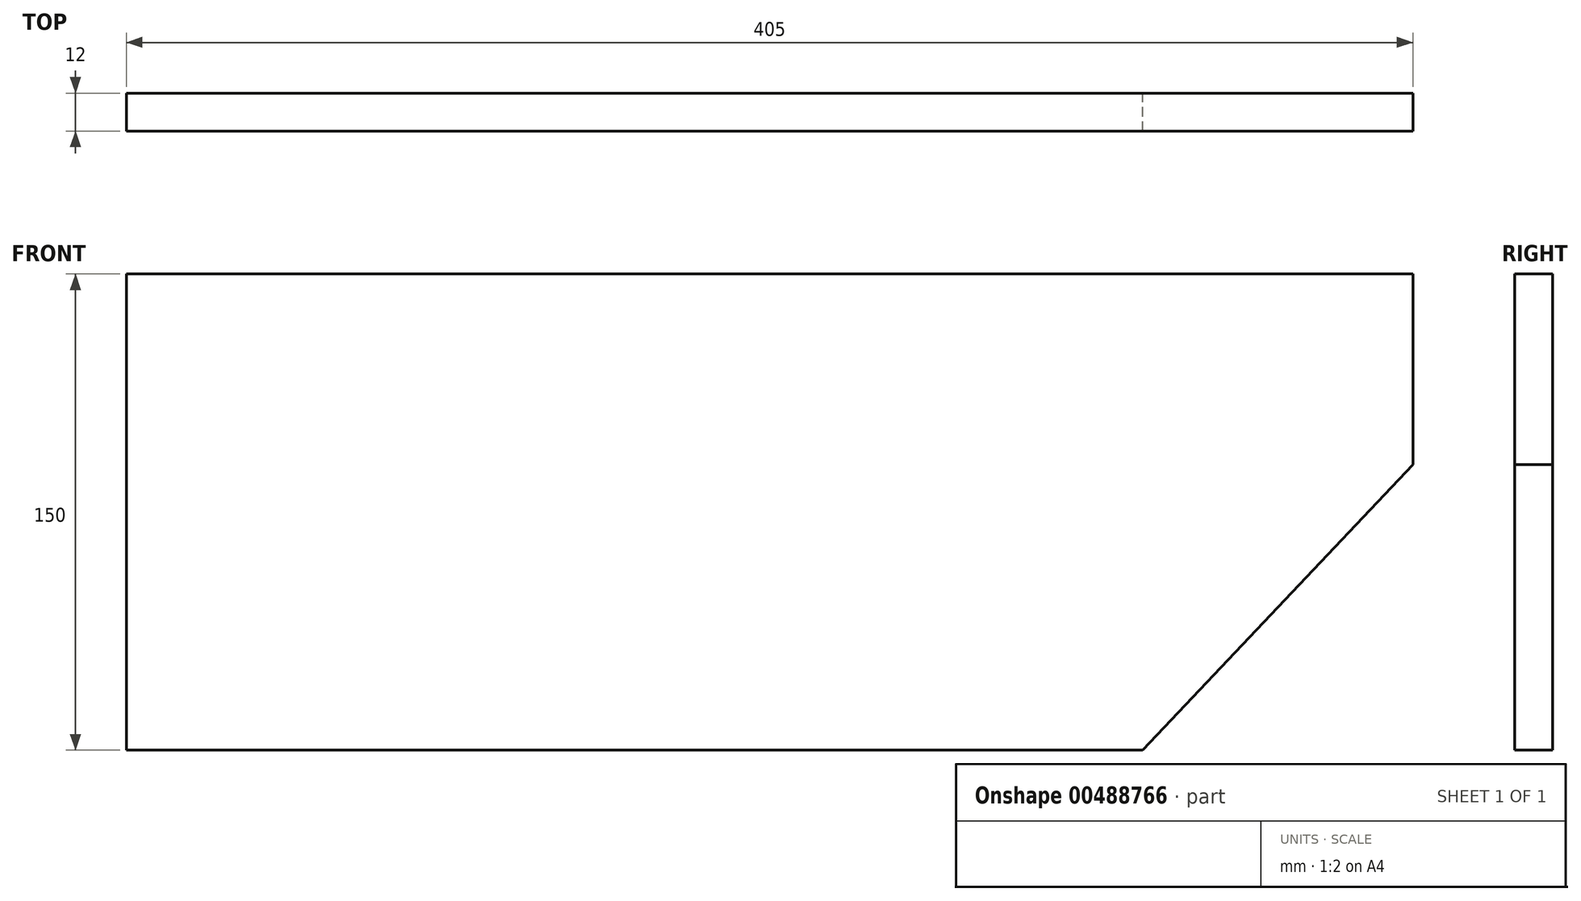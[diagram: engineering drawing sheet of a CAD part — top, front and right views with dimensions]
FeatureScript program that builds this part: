
annotation { "Feature Type Name" : "Feature", "Feature Type Description" : "" }
export const myFeature = defineFeature(function(context is Context, id is Id, definition is map)
    precondition{}
    {
        {
            var Q0;
            Q0=qCreatedBy(makeId("Front.planeOp"),FACE);
            var sketch = newSketch(context, id + "F0", { "sketchPlane" : qUnion([Q0])});
            skLineSegment(sketch, "E0.bottom", {"start": v(-202.5, 75) * mm, "end": v(202.5, 75) * mm});
            skLineSegment(sketch, "E0.top", {"start": v(-202.5, -75) * mm, "end": v(202.5, -75) * mm});
            skLineSegment(sketch, "E0.left", {"start": v(-202.5, 75) * mm, "end": v(-202.5, -75) * mm});
            skLineSegment(sketch, "E0.right", {"start": v(202.5, 75) * mm, "end": v(202.5, -75) * mm});
            skLineSegment(sketch, "E1", {"start": v(-202.5, 75) * mm, "end": v(202.5, -75) * mm, "construction": true});
            skLineSegment(sketch, "E2.bottom", {"start": v(-202.5, 75) * mm, "end": v(-152.5, 75) * mm});
            skLineSegment(sketch, "E2.top", {"start": v(-202.5, 115) * mm, "end": v(-152.5, 115) * mm});
            skLineSegment(sketch, "E2.left", {"start": v(-202.5, 75) * mm, "end": v(-202.5, 115) * mm});
            skLineSegment(sketch, "E2.right", {"start": v(-152.5, 75) * mm, "end": v(-152.5, 115) * mm});
            skLineSegment(sketch, "E3", {"start": v(202.5, 15) * mm, "end": v(117.5, -75) * mm});
            skSolve(sketch);
        }
        {
            var Q0;
            Q0=makeQuery(id+"F0.imprint","IMPRINT",FACE,{"disambiguationData":[TD([[makeQuery(id+"F0.imprint","IMPRINT",EDGE,{"derivedFrom":sQuery(id+"F0.wireOp",EDGE,"E2.bottom")}),1.0]])]});
            var Q1;
            {var subQ1=sQuery(id+"F0.wireOp",EDGE,"E0.bottom");Q1=makeQuery(id+"F0.imprint","IMPRINT",FACE,{"disambiguationData":[TD([[makeQuery(id+"F0.imprint","IMPRINT",EDGE,{"derivedFrom":subQ1}),-1.0]])]});}
            extrude(context, id + "F1", {"entities" : qUnion([Q0, Q1]), "depth" : 12 * mm});
        }
    });
